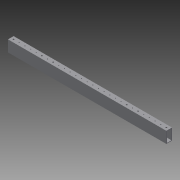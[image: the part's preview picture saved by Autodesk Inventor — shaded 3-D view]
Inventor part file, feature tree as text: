
AUTODESK INVENTOR PART (.ipt)
format: ipt  version: 2015 SP1 (Build 190203100, 203)  size: 176,128 bytes
history: native  units: in
note: dims shown in document units (in); Inventor stores cm internally (conversion verified against a paired STEP export)
features: sketch x3, extrude x2, projected_geometry x2, hole x1, pattern_linear x1
ambient origin geometry x8: Origin, YZ Plane, XZ Plane, XY Plane, X Axis, Y Axis, Z Axis, Center Point
bodies: Solid1 (feature_tree)
feature tree (9):
  extrude  "Extrusion1"  Depth=1.0in
  hole  "Hole1"  [1 undecoded]
  pattern_linear  "Rectangular Pattern1"  Spacing1=0.1in  [1 undecoded]
  extrude  "Extrusion3"  Depth=28.0in TaperAngle=0.0deg
  sketch  "Sketch1"  dims[d0=2.0in d1=1.0in]
  sketch  "Sketch2"  dims[d2=1.8in d3=0.8in]
  projected_geometry  "Projected Loop1"
  sketch  "Sketch4"  dims[d4=0.1in d5=0.1in d6=28.0in d7=0.0in d9=0.5in d10=0.5in d11=0.1562in d12=0.75in d13=0.375in d14=0.25in d15=0.5635in d16=1.0in d17=0.8108in d18=11.0236in d20=1.0in d27=0.25in d28=0.25in d29=0.25in d30=0.25in d31=0.25in d32=0.25in d33=1.0in d34=0.0in]
  projected_geometry  "Projected Loop3"
note: 2 required parameter values undecoded (feature->parameter linkage not recoverable at this tier; creation-order binding heuristic only, values carry confidence <= 0.55)
